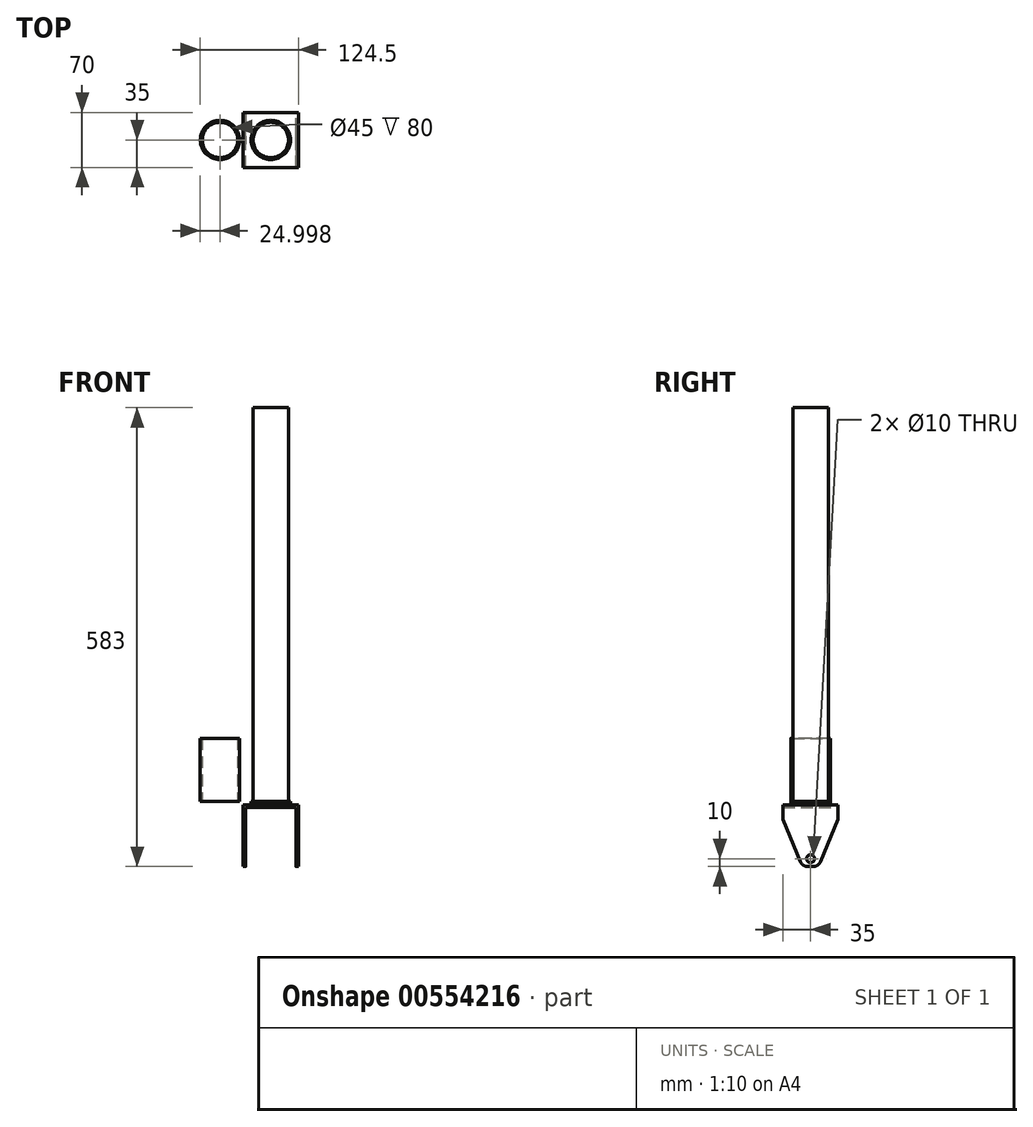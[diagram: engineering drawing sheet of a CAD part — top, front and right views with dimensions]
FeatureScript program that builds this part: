
annotation { "Feature Type Name" : "Feature", "Feature Type Description" : "" }
export const myFeature = defineFeature(function(context is Context, id is Id, definition is map)
    precondition{}
    {
        {
            var Q0;
            Q0=qCreatedBy(makeId("Top.planeOp"),FACE);
            var sketch = newSketch(context, id + "F0", { "sketchPlane" : qUnion([Q0])});
            skCircle(sketch, "E0", {"center": v(-100.15, 0) * mm, "radius": 25 * mm});
            skCircle(sketch, "E1", {"center": v(-100.15, 0) * mm, "radius": 22.5 * mm});
            skSolve(sketch);
        }
        {
            var Q0;
            Q0=makeQuery(id+"F0.imprint","IMPRINT",FACE,{"disambiguationData":[TD([[makeQuery(id+"F0.imprint","IMPRINT",EDGE,{"derivedFrom":sQuery(id+"F0.wireOp",EDGE,"E0")}),1.0]])]});
            extrude(context, id + "F1", {"entities" : qUnion([Q0]), "depth" : 80 * mm, "offsetDistance" : 25 * mm});
        }
        {
            var Q0;
            Q0=qCreatedBy(makeId("Top.planeOp"),FACE);
            var sketch = newSketch(context, id + "F2", { "sketchPlane" : qUnion([Q0])});
            skCircle(sketch, "E2", {"center": v(-35.65, 0) * mm, "radius": 22.5 * mm});
            skSolve(sketch);
        }
        {
            var Q0;
            Q0=makeQuery(id+"F2.imprint","IMPRINT",FACE,{"disambiguationData":[TD([[makeQuery(id+"F2.imprint","IMPRINT",EDGE,{"derivedFrom":sQuery(id+"F2.wireOp",EDGE,"E2")}),1.0]])]});
            extrude(context, id + "F3", {"entities" : qUnion([Q0]), "depth" : 500 * mm, "offsetDistance" : 25 * mm});
        }
        {
            var Q0;
            Q0=makeQuery(id+"F3.opExtrude","CAP_FACE",FACE,{"disambiguationData":[OSD([sQuery(id+"F2.wireOp",EDGE,"E2")])],"isStart":true});
            var sketch = newSketch(context, id + "F4", { "sketchPlane" : qUnion([Q0])});
            skCircle(sketch, "E3", {"center": v(-35.65, 0) * mm, "radius": 25 * mm});
            skSolve(sketch);
        }
        {
            var Q0;
            Q0 = qSketchRegion(id + "F4", true);
            extrude(context, id + "F5", {"entities" : qUnion([Q0]), "operationType" : NewBodyOperationType.ADD, "depth" : 5 * mm, "offsetDistance" : 25 * mm});
        }
        {
            var Q0;
            Q0=makeQuery(id+"F5.opExtrude","CAP_FACE",FACE,{"disambiguationData":[OSD([sQuery(id+"F4.wireOp",EDGE,"E3")])],"isStart":false});
            var sketch = newSketch(context, id + "F6", { "sketchPlane" : qUnion([Q0])});
            skLineSegment(sketch, "E4.bottom", {"start": v(-0.65, -35) * mm, "end": v(-70.65, -35) * mm});
            skLineSegment(sketch, "E4.top", {"start": v(-0.65, 35) * mm, "end": v(-70.65, 35) * mm});
            skLineSegment(sketch, "E4.left", {"start": v(-0.65, -35) * mm, "end": v(-0.65, 35) * mm});
            skLineSegment(sketch, "E4.right", {"start": v(-70.65, -35) * mm, "end": v(-70.65, 35) * mm});
            skPoint(sketch, "E4.middle", {"position": v(-35.65, 0) * mm});
            skSolve(sketch);
        }
        {
            var Q0;
            Q0 = qSketchRegion(id + "F6", true);
            extrude(context, id + "F7", {"entities" : qUnion([Q0]), "operationType" : NewBodyOperationType.ADD, "depth" : 3 * mm, "offsetDistance" : 25 * mm});
        }
        {
            var Q0;
            Q0=makeQuery(id+"F7.opExtrude","CAP_FACE",FACE,{"disambiguationData":[OSD([sQuery(id+"F6.wireOp",EDGE,"E4.bottom"),sQuery(id+"F6.wireOp",EDGE,"E4.top"),sQuery(id+"F6.wireOp",EDGE,"E4.left"),sQuery(id+"F6.wireOp",EDGE,"E4.right")])],"isStart":false});
            var sketch = newSketch(context, id + "F8", { "sketchPlane" : qUnion([Q0])});
            skLineSegment(sketch, "E5.bottom", {"start": v(-70.65, 35) * mm, "end": v(-67.65, 35) * mm});
            skLineSegment(sketch, "E5.top", {"start": v(-70.65, -35) * mm, "end": v(-67.65, -35) * mm});
            skLineSegment(sketch, "E5.left", {"start": v(-70.65, 35) * mm, "end": v(-70.65, -35) * mm});
            skLineSegment(sketch, "E5.right", {"start": v(-67.65, 35) * mm, "end": v(-67.65, -35) * mm});
            skLineSegment(sketch, "E6.bottom", {"start": v(-0.65, 35) * mm, "end": v(-3.65, 35) * mm});
            skLineSegment(sketch, "E6.top", {"start": v(-0.65, -35) * mm, "end": v(-3.65, -35) * mm});
            skLineSegment(sketch, "E6.left", {"start": v(-0.65, 35) * mm, "end": v(-0.65, -35) * mm});
            skLineSegment(sketch, "E6.right", {"start": v(-3.65, 35) * mm, "end": v(-3.65, -35) * mm});
            skSolve(sketch);
        }
        {
            var Q0;
            Q0 = qSketchRegion(id + "F8", true);
            extrude(context, id + "F9", {"entities" : qUnion([Q0]), "operationType" : NewBodyOperationType.ADD, "depth" : 75 * mm, "offsetDistance" : 25 * mm});
        }
        {
            var Q0;
            Q0=makeQuery(id+"F9.opExtrude","CAP_EDGE",EDGE,{"disambiguationData":[OSD([sQuery(id+"F8.wireOp",EDGE,"E5.bottom")])],"isStart":false});
            var Q1;
            Q1=makeQuery(id+"F9.opExtrude","CAP_EDGE",EDGE,{"disambiguationData":[OSD([sQuery(id+"F8.wireOp",EDGE,"E5.top")])],"isStart":false});
            chamfer(context, id + "F10", {"entities" : qUnion([Q0, Q1]), "chamferType" : ChamferType.TWO_OFFSETS, "width1" : 25 * mm, "oppositeDirection" : false, "width2" : 60 * mm, "tangentPropagation" : true});
        }
        {
            var Q0;
            Q0=makeQuery(id+"F9.opExtrude","CAP_EDGE",EDGE,{"disambiguationData":[OSD([sQuery(id+"F8.wireOp",EDGE,"E6.top")])],"isStart":false});
            var Q1;
            Q1=makeQuery(id+"F9.opExtrude","CAP_EDGE",EDGE,{"disambiguationData":[OSD([sQuery(id+"F8.wireOp",EDGE,"E6.bottom")])],"isStart":false});
            chamfer(context, id + "F11", {"entities" : qUnion([Q0, Q1]), "chamferType" : ChamferType.TWO_OFFSETS, "width1" : 25 * mm, "oppositeDirection" : true, "width2" : 60 * mm, "tangentPropagation" : true});
        }
        {
            var Q0;
            Q0=makeQuery(id+"F9.boolean.opBoolean","MERGE",FACE,{"derivedFrom":[makeQuery(id+"F7.opExtrude","SWEPT_FACE",FACE,{"disambiguationData":[OSD([sQuery(id+"F6.wireOp",EDGE,"E4.left")])]}),makeQuery(id+"F9.opExtrude","SWEPT_FACE",FACE,{"disambiguationData":[OSD([sQuery(id+"F8.wireOp",EDGE,"E6.left")])]})]});
            var sketch = newSketch(context, id + "F12", { "sketchPlane" : qUnion([Q0])});
            skPoint(sketch, "E7", {"position": v(0, -73) * mm});
            skSolve(sketch);
        }
        {
            var Q0;
            Q0=sQuery(id+"F12.wireOp",VERTEX,"E7");
            var Q1;
            Q1=makeQuery(id+"F3.opExtrude","SWEPT_BODY",BODY,{"disambiguationData":[OSD([sQuery(id+"F2.wireOp",EDGE,"E2")])]});
            hole(context, id + "F13", {"style" : HoleStyle.SIMPLE, "endStyle" : HoleEndStyle.THROUGH, "holeDiameter" : 10 * mm, "isTappedThrough" : true, "tappedDepth" : 12 * mm, "tapClearance" : 3, "locations" : qUnion([Q0]), "scope" : qUnion([Q1])});
        }
        {
            var Q0;
            {var subQ0=sQuery(id+"F8.wireOp",EDGE,"E6.top");Q0=makeQuery(id+"F11.opChamfer","BLEND_EDGE",EDGE,{"blendedFrom":[makeQuery(id+"F9.opExtrude","CAP_EDGE",EDGE,{"disambiguationData":[OSD([subQ0])],"isStart":false}),makeQuery(id+"F9.opExtrude","CAP_FACE",FACE,{"disambiguationData":[OSD([sQuery(id+"F8.wireOp",EDGE,"E6.bottom"),subQ0,sQuery(id+"F8.wireOp",EDGE,"E6.left"),sQuery(id+"F8.wireOp",EDGE,"E6.right")])],"isStart":false})],"blendedInto":[makeQuery(id+"F9.opExtrude","CAP_FACE",FACE,{"disambiguationData":[OSD([sQuery(id+"F8.wireOp",EDGE,"E6.bottom"),subQ0,sQuery(id+"F8.wireOp",EDGE,"E6.left"),sQuery(id+"F8.wireOp",EDGE,"E6.right")])],"isStart":false})]});}
            var Q1;
            {var subQ0=sQuery(id+"F8.wireOp",EDGE,"E6.bottom");Q1=makeQuery(id+"F11.opChamfer","BLEND_EDGE",EDGE,{"blendedFrom":[makeQuery(id+"F9.opExtrude","CAP_EDGE",EDGE,{"disambiguationData":[OSD([subQ0])],"isStart":false}),makeQuery(id+"F9.opExtrude","CAP_FACE",FACE,{"disambiguationData":[OSD([subQ0,sQuery(id+"F8.wireOp",EDGE,"E6.top"),sQuery(id+"F8.wireOp",EDGE,"E6.left"),sQuery(id+"F8.wireOp",EDGE,"E6.right")])],"isStart":false})],"blendedInto":[makeQuery(id+"F9.opExtrude","CAP_FACE",FACE,{"disambiguationData":[OSD([subQ0,sQuery(id+"F8.wireOp",EDGE,"E6.top"),sQuery(id+"F8.wireOp",EDGE,"E6.left"),sQuery(id+"F8.wireOp",EDGE,"E6.right")])],"isStart":false})]});}
            var Q2;
            {var subQ0=sQuery(id+"F8.wireOp",EDGE,"E5.bottom");Q2=makeQuery(id+"F10.opChamfer","BLEND_EDGE",EDGE,{"blendedFrom":[makeQuery(id+"F9.opExtrude","CAP_EDGE",EDGE,{"disambiguationData":[OSD([subQ0])],"isStart":false}),makeQuery(id+"F9.opExtrude","CAP_FACE",FACE,{"disambiguationData":[OSD([subQ0,sQuery(id+"F8.wireOp",EDGE,"E5.top"),sQuery(id+"F8.wireOp",EDGE,"E5.left"),sQuery(id+"F8.wireOp",EDGE,"E5.right")])],"isStart":false})],"blendedInto":[makeQuery(id+"F9.opExtrude","CAP_FACE",FACE,{"disambiguationData":[OSD([subQ0,sQuery(id+"F8.wireOp",EDGE,"E5.top"),sQuery(id+"F8.wireOp",EDGE,"E5.left"),sQuery(id+"F8.wireOp",EDGE,"E5.right")])],"isStart":false})]});}
            var Q3;
            {var subQ0=sQuery(id+"F8.wireOp",EDGE,"E5.top");Q3=makeQuery(id+"F10.opChamfer","BLEND_EDGE",EDGE,{"blendedFrom":[makeQuery(id+"F9.opExtrude","CAP_EDGE",EDGE,{"disambiguationData":[OSD([subQ0])],"isStart":false}),makeQuery(id+"F9.opExtrude","CAP_FACE",FACE,{"disambiguationData":[OSD([sQuery(id+"F8.wireOp",EDGE,"E5.bottom"),subQ0,sQuery(id+"F8.wireOp",EDGE,"E5.left"),sQuery(id+"F8.wireOp",EDGE,"E5.right")])],"isStart":false})],"blendedInto":[makeQuery(id+"F9.opExtrude","CAP_FACE",FACE,{"disambiguationData":[OSD([sQuery(id+"F8.wireOp",EDGE,"E5.bottom"),subQ0,sQuery(id+"F8.wireOp",EDGE,"E5.left"),sQuery(id+"F8.wireOp",EDGE,"E5.right")])],"isStart":false})]});}
            fillet(context, id + "F14", {"entities" : qUnion([Q0, Q1, Q2, Q3]), "radius" : 10 * mm, "tangentPropagation" : true, "allowEdgeOverflow" : false});
        }
    });
